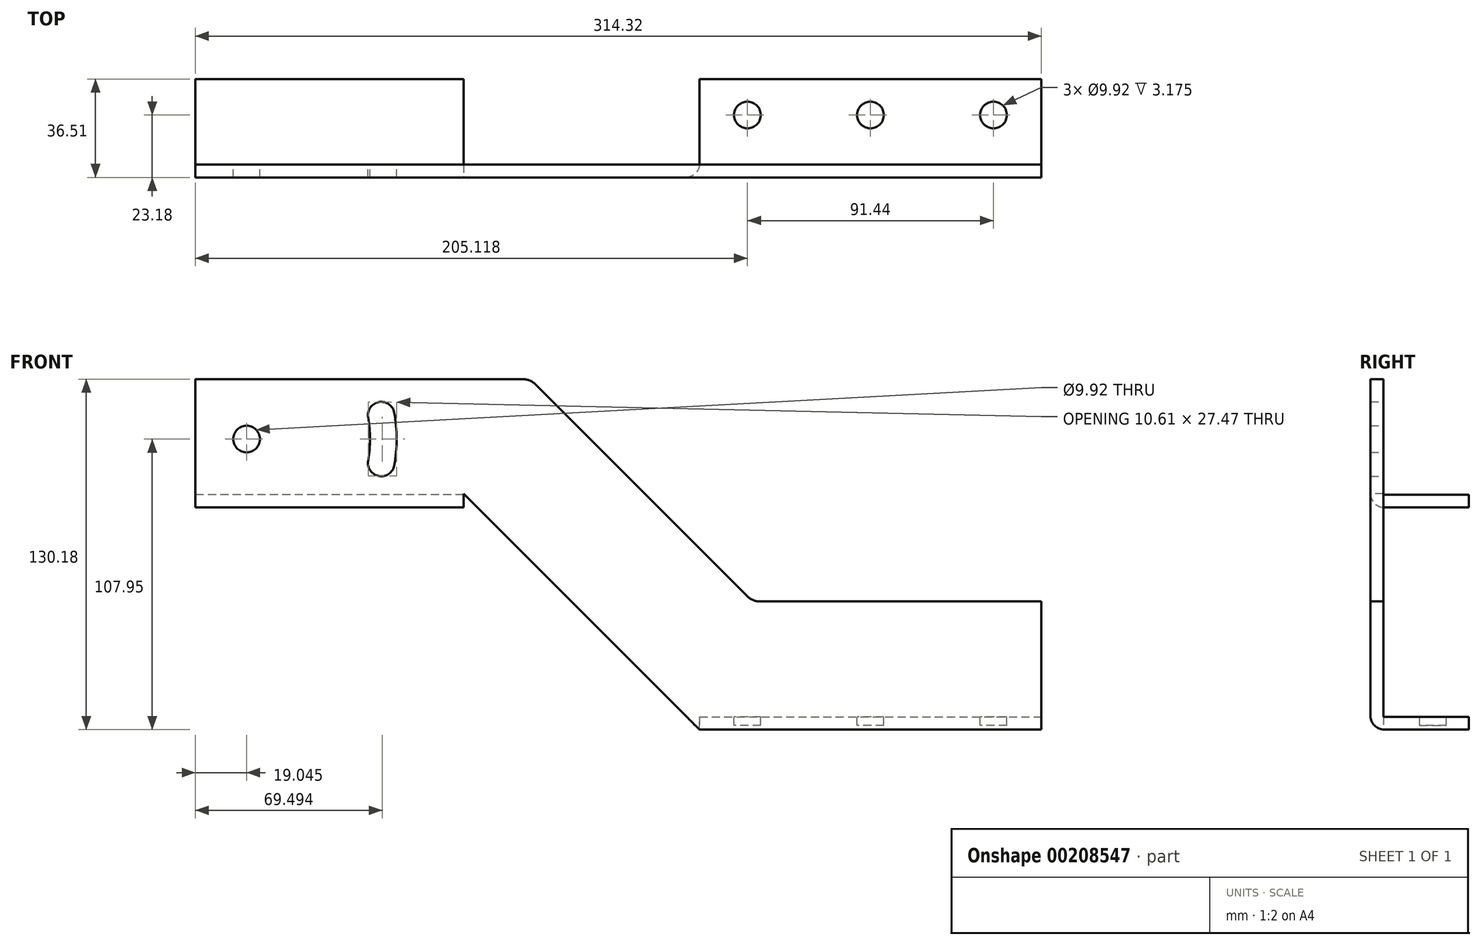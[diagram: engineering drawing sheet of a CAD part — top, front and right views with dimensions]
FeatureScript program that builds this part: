
annotation { "Feature Type Name" : "Feature", "Feature Type Description" : "" }
export const myFeature = defineFeature(function(context is Context, id is Id, definition is map)
    precondition{}
    {
        {
            var Q0;
            Q0=qCreatedBy(makeId("Front.planeOp"),FACE);
            var sketch = newSketch(context, id + "F0", { "sketchPlane" : qUnion([Q0])});
            skLineSegment(sketch, "E0", {"start": v(0, 0) * mm, "end": v(127, 0) * mm});
            skLineSegment(sketch, "E1", {"start": v(0, 0) * mm, "end": v(-82.55, 82.55) * mm});
            skLineSegment(sketch, "E2", {"start": v(-82.55, 82.55) * mm, "end": v(-187.33, 82.55) * mm});
            skLineSegment(sketch, "E3.0", {"start": v(-65.45, 130.17) * mm, "end": v(-187.33, 130.17) * mm});
            skLineSegment(sketch, "E3.1", {"start": v(17.87, 49.48) * mm, "end": v(-60.96, 128.32) * mm});
            skLineSegment(sketch, "E3.2", {"start": v(22.36, 47.63) * mm, "end": v(127, 47.63) * mm});
            skLineSegment(sketch, "E4", {"start": v(-187.33, 130.17) * mm, "end": v(-187.33, 82.55) * mm});
            skLineSegment(sketch, "E5", {"start": v(127, 47.62) * mm, "end": v(127, 0) * mm});
            skCircle(sketch, "E6", {"center": v(-168.28, 107.95) * mm, "radius": 4.96 * mm});
            skLineSegment(sketch, "E7.direction1", {"start": v(-168.28, 107.95) * mm, "end": v(-117.47, 107.95) * mm, "construction": true});
            skPoint(sketch, "E8.visualSharp", {"position": v(-62.82, 130.17) * mm});
            skArc(sketch, "E8.filletArc", {"start": v(-60.96, 128.32) * mm, "mid": v(-63.02, 129.7) * mm, "end": v(-65.45, 130.17) * mm});
            skPoint(sketch, "E9.visualSharp", {"position": v(19.73, 47.63) * mm});
            skArc(sketch, "E9.filletArc", {"start": v(17.87, 49.48) * mm, "mid": v(19.93, 48.1) * mm, "end": v(22.36, 47.63) * mm});
            skPoint(sketch, "E10.visualSharp", {"position": v(-82.55, 82.55) * mm});
            skPoint(sketch, "E11.visualSharp", {"position": v(-187.33, 130.17) * mm});
            skPoint(sketch, "E12.visualSharp", {"position": v(-187.33, 82.55) * mm});
            skPoint(sketch, "E13.visualSharp", {"position": v(127, 47.63) * mm});
            skPoint(sketch, "E14.visualSharp", {"position": v(127, 0) * mm});
            skArc(sketch, "E15", {"start": v(-117.47, 107.95) * mm, "mid": v(-117.67, 112.4) * mm, "end": v(-118.25, 116.8) * mm, "construction": true});
            skArc(sketch, "E16", {"start": v(-117.47, 107.95) * mm, "mid": v(-117.67, 103.5) * mm, "end": v(-118.25, 99.1) * mm, "construction": true});
            skArc(sketch, "E17.0", {"start": v(-112.52, 107.95) * mm, "mid": v(-112.74, 112.83) * mm, "end": v(-113.38, 117.67) * mm});
            skArc(sketch, "E17.1", {"start": v(-112.52, 107.95) * mm, "mid": v(-112.74, 103.07) * mm, "end": v(-113.38, 98.23) * mm});
            skArc(sketch, "E18.0", {"start": v(-122.43, 107.95) * mm, "mid": v(-122.6, 111.96) * mm, "end": v(-123.13, 115.94) * mm});
            skArc(sketch, "E18.1", {"start": v(-122.43, 107.95) * mm, "mid": v(-122.6, 103.94) * mm, "end": v(-123.13, 99.96) * mm});
            skArc(sketch, "E19", {"start": v(-123.13, 115.94) * mm, "mid": v(-119.12, 121.68) * mm, "end": v(-113.38, 117.67) * mm});
            skArc(sketch, "E20", {"start": v(-123.13, 99.96) * mm, "mid": v(-119.12, 94.22) * mm, "end": v(-113.38, 98.23) * mm});
            skSolve(sketch);
        }
        {
            var Q0;
            Q0=makeQuery(id+"F0.imprint","IMPRINT",FACE,{"disambiguationData":[TD([[makeQuery(id+"F0.imprint","IMPRINT",EDGE,{"derivedFrom":sQuery(id+"F0.wireOp",EDGE,"E0")}),1.0]])]});
            extrude(context, id + "F1", {"entities" : qUnion([Q0]), "depth" : 4.76 * mm});
        }
        {
            var Q0;
            Q0=makeQuery(id+"F1.opExtrude","SWEPT_FACE",FACE,{"disambiguationData":[OSD([sQuery(id+"F0.wireOp",EDGE,"E5")])]});
            var sketch = newSketch(context, id + "F2", { "sketchPlane" : qUnion([Q0])});
            skLineSegment(sketch, "E21.bottom", {"start": v(0, 0) * mm, "end": v(31.75, 0) * mm});
            skLineSegment(sketch, "E21.top", {"start": v(0, 4.76) * mm, "end": v(31.75, 4.76) * mm});
            skLineSegment(sketch, "E21.left", {"start": v(0, 0) * mm, "end": v(0, 4.76) * mm});
            skLineSegment(sketch, "E21.right", {"start": v(31.75, 0) * mm, "end": v(31.75, 4.76) * mm});
            skSolve(sketch);
        }
        {
            var Q0;
            Q0 = qSketchRegion(id + "F2", true);
            extrude(context, id + "F3", {"entities" : qUnion([Q0]), "operationType" : NewBodyOperationType.ADD, "oppositeDirection" : true, "depth" : 127 * mm});
        }
        {
            var Q0;
            Q0=makeQuery(id+"F1.opExtrude","CAP_EDGE",EDGE,{"disambiguationData":[OSD([sQuery(id+"F0.wireOp",EDGE,"E0")])],"isStart":false});
            var Q1;
            Q1=makeQuery(id+"F3.opExtrude","SWEPT_EDGE",EDGE,{"disambiguationData":[OSD([sQuery(id+"F0.wireOp",EDGE,"E5"),sQuery(id+"F2.wireOp",EDGE,"E21.top"),sQuery(id+"F2.wireOp",EDGE,"E21.left")])]});
            fillet(context, id + "F4", {"entities" : qUnion([Q0, Q1]), "radius" : 5.08 * mm, "tangentPropagation" : true, "allowEdgeOverflow" : false});
        }
        {
            var Q0;
            Q0=makeQuery(id+"F3.opExtrude","SWEPT_FACE",FACE,{"disambiguationData":[OSD([sQuery(id+"F2.wireOp",EDGE,"E21.top")])]});
            var sketch = newSketch(context, id + "F5", { "sketchPlane" : qUnion([Q0])});
            skCircle(sketch, "E22", {"center": v(17.8, 18.42) * mm, "radius": 4.96 * mm});
            skCircle(sketch, "E23.1.0.0", {"center": v(63.52, 18.42) * mm, "radius": 4.96 * mm});
            skCircle(sketch, "E23.2.0.0", {"center": v(109.24, 18.42) * mm, "radius": 4.96 * mm});
            skLineSegment(sketch, "E23.direction1", {"start": v(17.8, 18.42) * mm, "end": v(63.52, 18.42) * mm, "construction": true});
            skSolve(sketch);
        }
        {
            var Q0;
            Q0 = qSketchRegion(id + "F5", true);
            extrude(context, id + "F6", {"entities" : qUnion([Q0]), "operationType" : NewBodyOperationType.REMOVE, "oppositeDirection" : true, "depth" : 3.17 * mm});
        }
        {
            var Q0;
            Q0=makeQuery(id+"F1.opExtrude","SWEPT_FACE",FACE,{"disambiguationData":[OSD([sQuery(id+"F0.wireOp",EDGE,"E4")])]});
            var sketch = newSketch(context, id + "F7", { "sketchPlane" : qUnion([Q0])});
            skLineSegment(sketch, "E24.bottom", {"start": v(0, 82.55) * mm, "end": v(-31.75, 82.55) * mm});
            skLineSegment(sketch, "E24.top", {"start": v(0, 87.31) * mm, "end": v(-31.75, 87.31) * mm});
            skLineSegment(sketch, "E24.left", {"start": v(0, 82.55) * mm, "end": v(0, 87.31) * mm});
            skLineSegment(sketch, "E24.right", {"start": v(-31.75, 82.55) * mm, "end": v(-31.75, 87.31) * mm});
            skSolve(sketch);
        }
        {
            var Q0;
            Q0 = qSketchRegion(id + "F7", true);
            extrude(context, id + "F8", {"entities" : qUnion([Q0]), "operationType" : NewBodyOperationType.ADD, "oppositeDirection" : true, "depth" : 99.7 * mm});
        }
        {
            var Q0;
            Q0=makeQuery(id+"F1.opExtrude","CAP_EDGE",EDGE,{"disambiguationData":[OSD([sQuery(id+"F0.wireOp",EDGE,"E2")])],"isStart":false});
            var Q1;
            Q1=makeQuery(id+"F8.opExtrude","SWEPT_EDGE",EDGE,{"disambiguationData":[OSD([sQuery(id+"F0.wireOp",EDGE,"E4"),sQuery(id+"F7.wireOp",EDGE,"E24.top"),sQuery(id+"F7.wireOp",EDGE,"E24.left")])]});
            fillet(context, id + "F9", {"entities" : qUnion([Q0, Q1]), "radius" : 5.08 * mm, "tangentPropagation" : true, "allowEdgeOverflow" : false});
        }
        {
            var Q0;
            Q0=makeQuery(id+"F1.opExtrude","CAP_FACE",FACE,{"disambiguationData":[OSD([sQuery(id+"F0.wireOp",EDGE,"E0"),sQuery(id+"F0.wireOp",EDGE,"E1"),sQuery(id+"F0.wireOp",EDGE,"E2"),sQuery(id+"F0.wireOp",EDGE,"E3.0"),sQuery(id+"F0.wireOp",EDGE,"E3.1"),sQuery(id+"F0.wireOp",EDGE,"E3.2"),sQuery(id+"F0.wireOp",EDGE,"E4"),sQuery(id+"F0.wireOp",EDGE,"E5"),sQuery(id+"F0.wireOp",EDGE,"E6"),sQuery(id+"F0.wireOp",EDGE,"E7.1.0.0"),sQuery(id+"F0.wireOp",EDGE,"E8.filletArc"),sQuery(id+"F0.wireOp",EDGE,"E9.filletArc")])],"isStart":false});
            var sketch = newSketch(context, id + "F10", { "sketchPlane" : qUnion([Q0])});
            skLineSegment(sketch, "E25", {"start": v(-87.63, 87.63) * mm, "end": v(-87.63, 82.56) * mm});
            skLineSegment(sketch, "E26", {"start": v(-87.63, 82.56) * mm, "end": v(-82.56, 82.56) * mm});
            skLineSegment(sketch, "E27", {"start": v(-82.56, 82.56) * mm, "end": v(-87.63, 87.63) * mm});
            skSolve(sketch);
        }
        {
            var Q0;
            Q0 = qSketchRegion(id + "F10", true);
            extrude(context, id + "F11", {"entities" : qUnion([Q0]), "operationType" : NewBodyOperationType.REMOVE, "oppositeDirection" : true, "depth" : 25.4 * mm});
        }
    });
